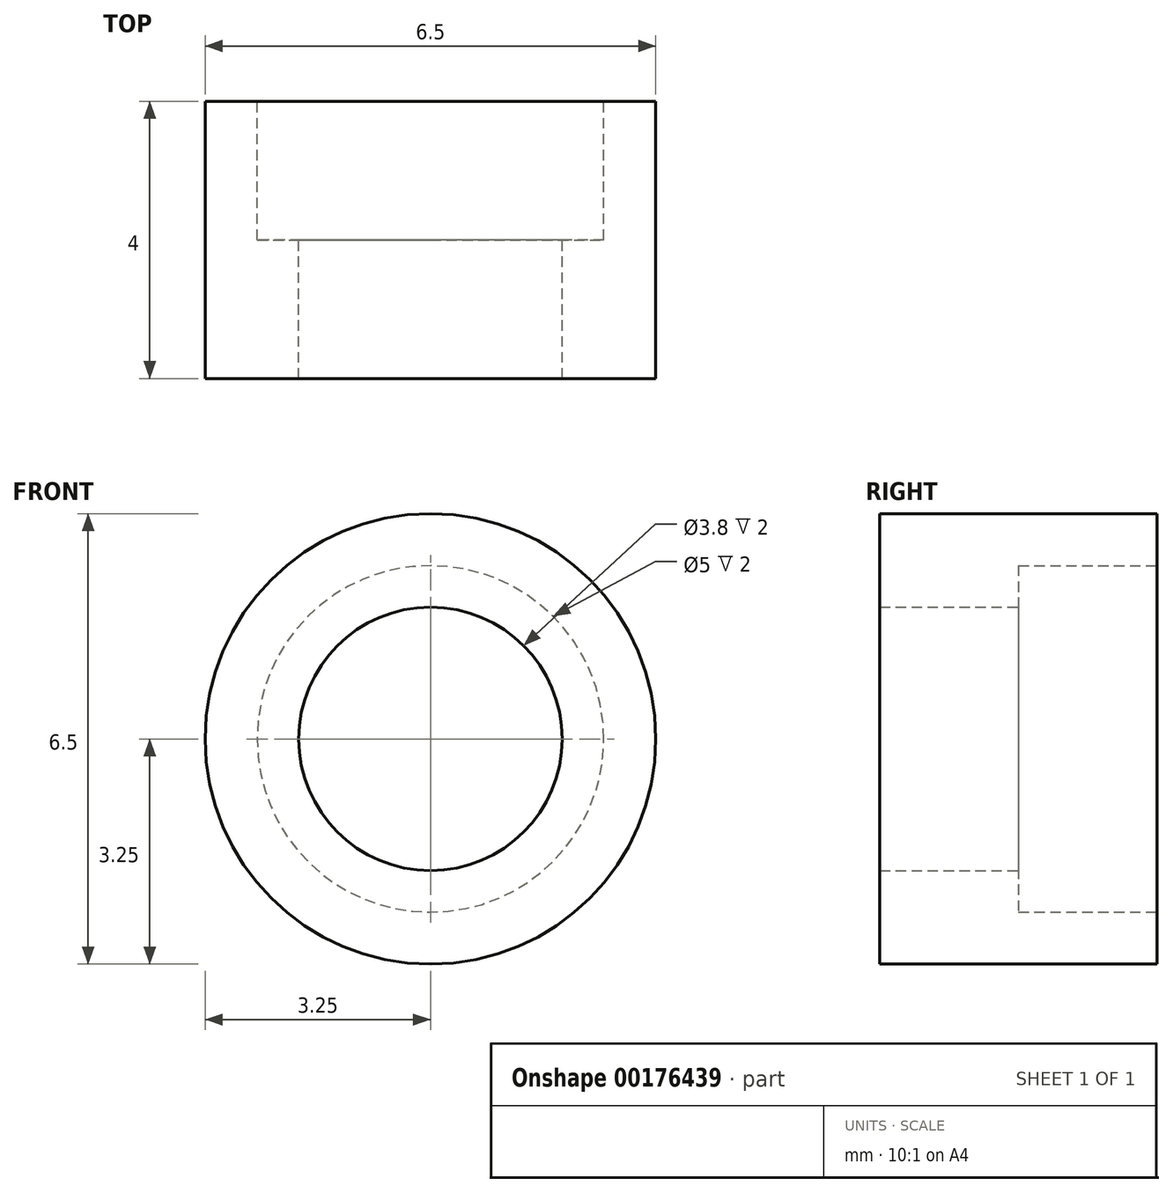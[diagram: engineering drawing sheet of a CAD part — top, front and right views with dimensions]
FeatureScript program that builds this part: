
annotation { "Feature Type Name" : "Feature", "Feature Type Description" : "" }
export const myFeature = defineFeature(function(context is Context, id is Id, definition is map)
    precondition{}
    {
        {
            var Q0;
            Q0=qCreatedBy(makeId("Right.planeOp"),FACE);
            var sketch = newSketch(context, id + "F0", { "sketchPlane" : qUnion([Q0])});
            skLineSegment(sketch, "E0", {"start": v(11.47, 0) * mm, "end": v(0, 0) * mm, "construction": true});
            skLineSegment(sketch, "E1", {"start": v(2, 1.9) * mm, "end": v(0, 1.9) * mm});
            skLineSegment(sketch, "E2", {"start": v(2, 1.9) * mm, "end": v(2, 2.5) * mm});
            skLineSegment(sketch, "E3", {"start": v(4, 2.5) * mm, "end": v(2, 2.5) * mm});
            skLineSegment(sketch, "E4", {"start": v(4, 2.5) * mm, "end": v(4, 3.25) * mm});
            skLineSegment(sketch, "E5", {"start": v(2, 3.25) * mm, "end": v(4, 3.25) * mm});
            skLineSegment(sketch, "E6", {"start": v(2, 3.25) * mm, "end": v(2, 3.25) * mm});
            skLineSegment(sketch, "E7", {"start": v(0, 3.25) * mm, "end": v(2, 3.25) * mm});
            skLineSegment(sketch, "E8", {"start": v(0, 3.25) * mm, "end": v(0, 1.9) * mm});
            skSolve(sketch);
        }
        {
            var Q0;
            Q0=makeQuery(id+"F0.imprint","IMPRINT",FACE,{"disambiguationData":[TD([[makeQuery(id+"F0.imprint","IMPRINT",EDGE,{"derivedFrom":sQuery(id+"F0.wireOp",EDGE,"E1")}),-1.0]])]});
            var Q1;
            Q1=sQuery(id+"F0.wireOp",EDGE,"E0");
            revolve(context, id + "F1", {"entities" : qUnion([Q0]), "axis" : qUnion([Q1]), "revolveType" : RevolveType.FULL});
        }
    });
